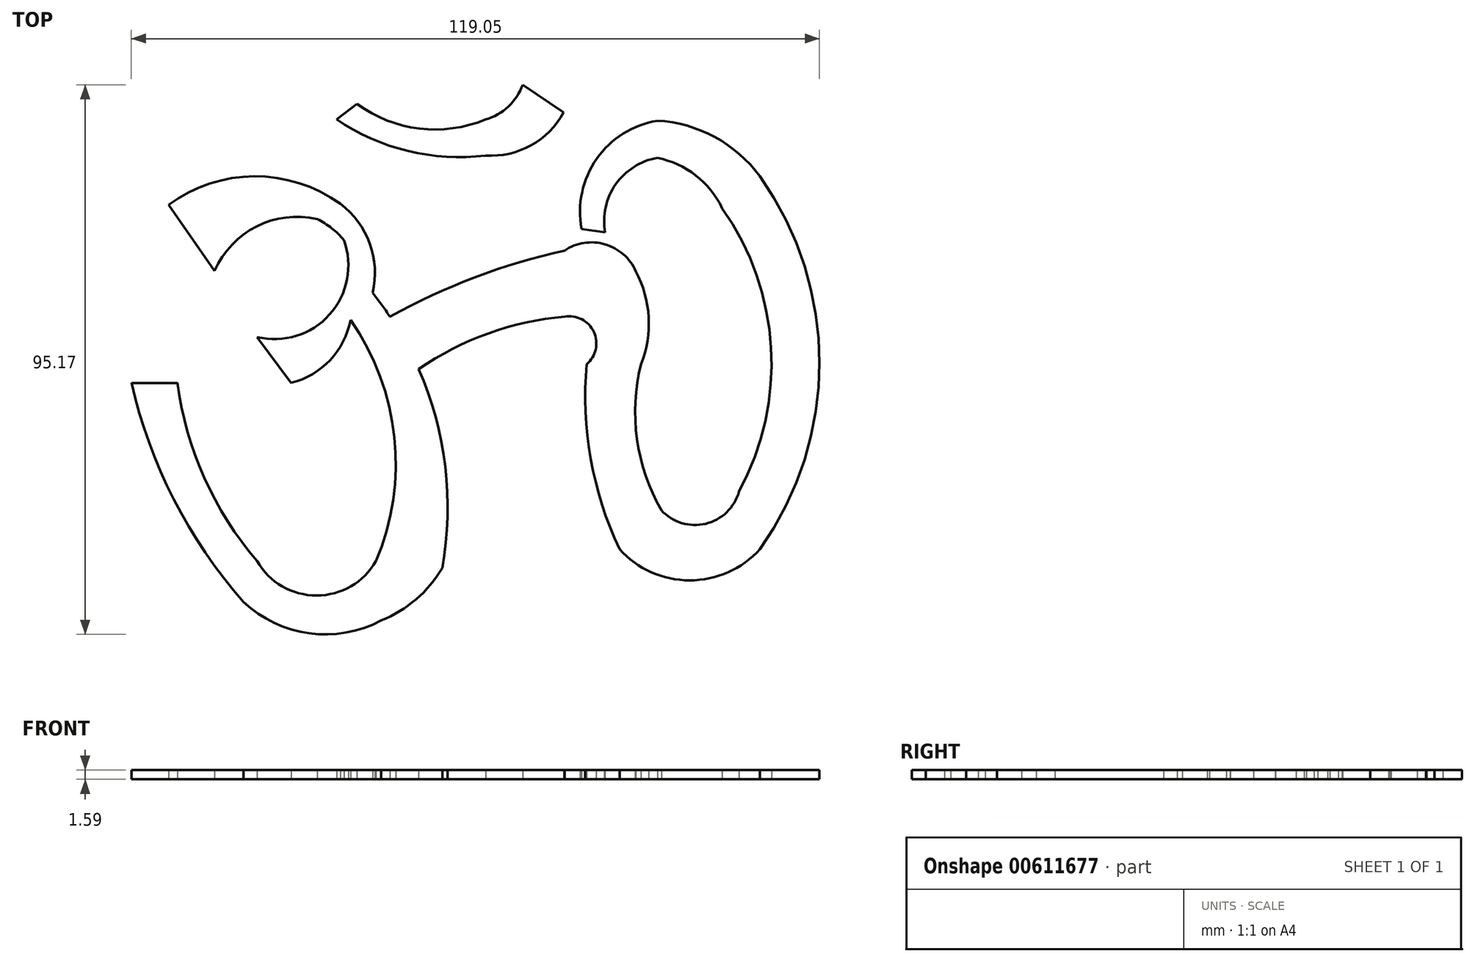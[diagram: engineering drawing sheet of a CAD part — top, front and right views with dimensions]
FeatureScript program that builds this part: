
annotation { "Feature Type Name" : "Feature", "Feature Type Description" : "" }
export const myFeature = defineFeature(function(context is Context, id is Id, definition is map)
    precondition{}
    {
        {
            var Q0;
            Q0=qCreatedBy(makeId("Top.planeOp"),FACE);
            var sketch = newSketch(context, id + "F0", { "sketchPlane" : qUnion([Q0])});
            skLineSegment(sketch, "E0", {"start": v(-54.8, 35.41) * mm, "end": v(-46.87, 23.95) * mm});
            skLineSegment(sketch, "E1", {"start": v(-39.53, 12.5) * mm, "end": v(-33.65, 4.56) * mm});
            skArc(sketch, "E2", {"start": v(-18.96, -26.3) * mm, "mid": v(-15.77, -4.87) * mm, "end": v(-23.36, 15.43) * mm});
            skArc(sketch, "E3", {"start": v(-39.53, -26.3) * mm, "mid": v(-29.24, -32.26) * mm, "end": v(-18.96, -26.3) * mm});
            skLineSegment(sketch, "E4", {"start": v(-53.34, 4.56) * mm, "end": v(-61.28, 4.56) * mm});
            skArc(sketch, "E5", {"start": v(-41.88, -33.36) * mm, "mid": v(-30.5, -38.8) * mm, "end": v(-18.07, -36.59) * mm});
            skArc(sketch, "E6", {"start": v(-7.5, -27.48) * mm, "mid": v(-8.37, -2.37) * mm, "end": v(-19.54, 20.13) * mm});
            skArc(sketch, "E7", {"start": v(-18.07, -36.59) * mm, "mid": v(-12.02, -32.92) * mm, "end": v(-7.5, -27.48) * mm});
            skArc(sketch, "E8", {"start": v(-25.13, 35.56) * mm, "mid": v(-40, 40.3) * mm, "end": v(-54.8, 35.41) * mm});
            skPoint(sketch, "E9", {"position": v(-19.54, 15.43) * mm});
            skArc(sketch, "E10", {"start": v(-33.65, 4.56) * mm, "mid": v(-26.92, 8.49) * mm, "end": v(-23.36, 15.43) * mm});
            skArc(sketch, "E11", {"start": v(-19.54, 20.13) * mm, "mid": v(-20.03, 28.68) * mm, "end": v(-25.13, 35.56) * mm});
            skArc(sketch, "E12", {"start": v(-53.34, 4.56) * mm, "mid": v(-48.65, -11.87) * mm, "end": v(-39.53, -26.3) * mm});
            skArc(sketch, "E13", {"start": v(-61.28, 4.56) * mm, "mid": v(-53.94, -15.61) * mm, "end": v(-41.88, -33.36) * mm});
            skArc(sketch, "E14", {"start": v(13.67, 16.02) * mm, "mid": v(0.45, 13.12) * mm, "end": v(-11.56, 6.92) * mm});
            skArc(sketch, "E15", {"start": v(17.49, 7.79) * mm, "mid": v(18.74, 13.37) * mm, "end": v(13.67, 16.02) * mm});
            skArc(sketch, "E16", {"start": v(17.49, 7.79) * mm, "mid": v(18.2, -8.6) * mm, "end": v(23.18, -24.25) * mm});
            skArc(sketch, "E17", {"start": v(23.18, -24.25) * mm, "mid": v(35.32, -29.63) * mm, "end": v(47.46, -24.25) * mm});
            skPoint(sketch, "E18", {"position": v(-39.74, 40.3) * mm});
            skPoint(sketch, "E18.positionSnap0", {"position": v(-40, 40.3) * mm});
            skArc(sketch, "E19", {"start": v(47.46, -24.25) * mm, "mid": v(57.77, 8.03) * mm, "end": v(47.46, 40.3) * mm});
            skArc(sketch, "E20", {"start": v(26.9, 7.79) * mm, "mid": v(26.2, -5.2) * mm, "end": v(30.42, -17.49) * mm});
            skArc(sketch, "E21", {"start": v(26, 23.85) * mm, "mid": v(20.68, 28.54) * mm, "end": v(13.67, 27.48) * mm});
            skArc(sketch, "E22", {"start": v(26.9, 7.79) * mm, "mid": v(28.23, 15.92) * mm, "end": v(26, 23.85) * mm});
            skArc(sketch, "E23", {"start": v(13.67, 27.48) * mm, "mid": v(-1.84, 22.82) * mm, "end": v(-16.54, 16.02) * mm});
            skArc(sketch, "E24", {"start": v(-29.13, 32.93) * mm, "mid": v(-39.61, 31.63) * mm, "end": v(-46.87, 23.95) * mm});
            skArc(sketch, "E25", {"start": v(-24.5, 29.25) * mm, "mid": v(-26.63, 31.33) * mm, "end": v(-29.13, 32.93) * mm});
            skArc(sketch, "E26", {"start": v(-39.53, 12.5) * mm, "mid": v(-27, 16.37) * mm, "end": v(-24.5, 29.25) * mm});
            skArc(sketch, "E27", {"start": v(47.46, 40.3) * mm, "mid": v(39.67, 47.12) * mm, "end": v(29.72, 49.94) * mm});
            skPoint(sketch, "E28.endSnap0", {"position": v(20.68, 28.54) * mm});
            skArc(sketch, "E29", {"start": v(40.94, 34.77) * mm, "mid": v(36.37, 40.47) * mm, "end": v(29.72, 43.5) * mm});
            skArc(sketch, "E30", {"start": v(30.42, -17.49) * mm, "mid": v(38.08, -19.83) * mm, "end": v(43.85, -14.27) * mm});
            skArc(sketch, "E31", {"start": v(43.85, -14.27) * mm, "mid": v(49.39, 10.67) * mm, "end": v(40.94, 34.77) * mm});
            skLineSegment(sketch, "E32", {"start": v(-25.77, 50.15) * mm, "end": v(-22.24, 52.86) * mm});
            skArc(sketch, "E33", {"start": v(-25.77, 50.15) * mm, "mid": v(-13.45, 44.7) * mm, "end": v(0, 43.92) * mm});
            skArc(sketch, "E34", {"start": v(0, 43.92) * mm, "mid": v(7.85, 45.66) * mm, "end": v(13.5, 51.4) * mm});
            skLineSegment(sketch, "E35", {"start": v(6.43, 56.18) * mm, "end": v(13.5, 51.4) * mm});
            skArc(sketch, "E36", {"start": v(-22.24, 52.86) * mm, "mid": v(-11.48, 48.59) * mm, "end": v(0, 50.15) * mm});
            skArc(sketch, "E37", {"start": v(0, 50.15) * mm, "mid": v(3.94, 52.39) * mm, "end": v(6.43, 56.18) * mm});
            skLineSegment(sketch, "E38", {"start": v(-8.06, 55.36) * mm, "end": v(-13.45, 60.75) * mm});
            skPoint(sketch, "E38.endSnap0", {"position": v(-13.45, 44.7) * mm});
            skLineSegment(sketch, "E39", {"start": v(-13.45, 60.75) * mm, "end": v(-8.06, 55.36) * mm});
            skLineSegment(sketch, "E40", {"start": v(-8.06, 55.36) * mm, "end": v(-2.68, 60.75) * mm});
            skLineSegment(sketch, "E41", {"start": v(-13.45, 60.75) * mm, "end": v(-8.06, 66.14) * mm});
            skLineSegment(sketch, "E42", {"start": v(-2.68, 60.75) * mm, "end": v(-8.06, 66.14) * mm});
            skArc(sketch, "E43", {"start": v(29.72, 43.5) * mm, "mid": v(22.52, 38.93) * mm, "end": v(20.68, 30.61) * mm});
            skArc(sketch, "E44", {"start": v(29.72, 49.94) * mm, "mid": v(19.23, 43.34) * mm, "end": v(16.62, 31.22) * mm});
            skLineSegment(sketch, "E45", {"start": v(16.62, 31.22) * mm, "end": v(20.68, 30.61) * mm});
            skSolve(sketch);
        }
        {
            var Q0;
            Q0=makeQuery(id+"F0.imprint","IMPRINT",FACE,{"disambiguationData":[TD([[makeQuery(id+"F0.imprint","IMPRINT",EDGE,{"derivedFrom":sQuery(id+"F0.wireOp",EDGE,"E0")}),1.0]])]});
            var Q1;
            {var subQ1=sQuery(id+"F0.wireOp",EDGE,"E14");Q1=makeQuery(id+"F0.imprint","IMPRINT",FACE,{"disambiguationData":[TD([[makeQuery(id+"F0.imprint","IMPRINT",EDGE,{"derivedFrom":subQ1}),-1.0]])]});}
            var Q2;
            Q2=makeQuery(id+"F0.imprint","IMPRINT",FACE,{"disambiguationData":[TD([[makeQuery(id+"F0.imprint","IMPRINT",EDGE,{"derivedFrom":sQuery(id+"F0.wireOp",EDGE,"E32")}),-1.0]])]});
            var Q3;
            Q3=makeQuery(id+"F0.imprint","IMPRINT",FACE,{"disambiguationData":[TD([[makeQuery(id+"F0.imprint","IMPRINT",EDGE,{"derivedFrom":sQuery(id+"F0.wireOp",EDGE,"E39")}),1.0]])]});
            extrude(context, id + "F1", {"entities" : qUnion([Q0, Q1, Q2, Q3]), "depth" : 1.59 * mm, "offsetDistance" : 25.4 * mm});
        }
    });
